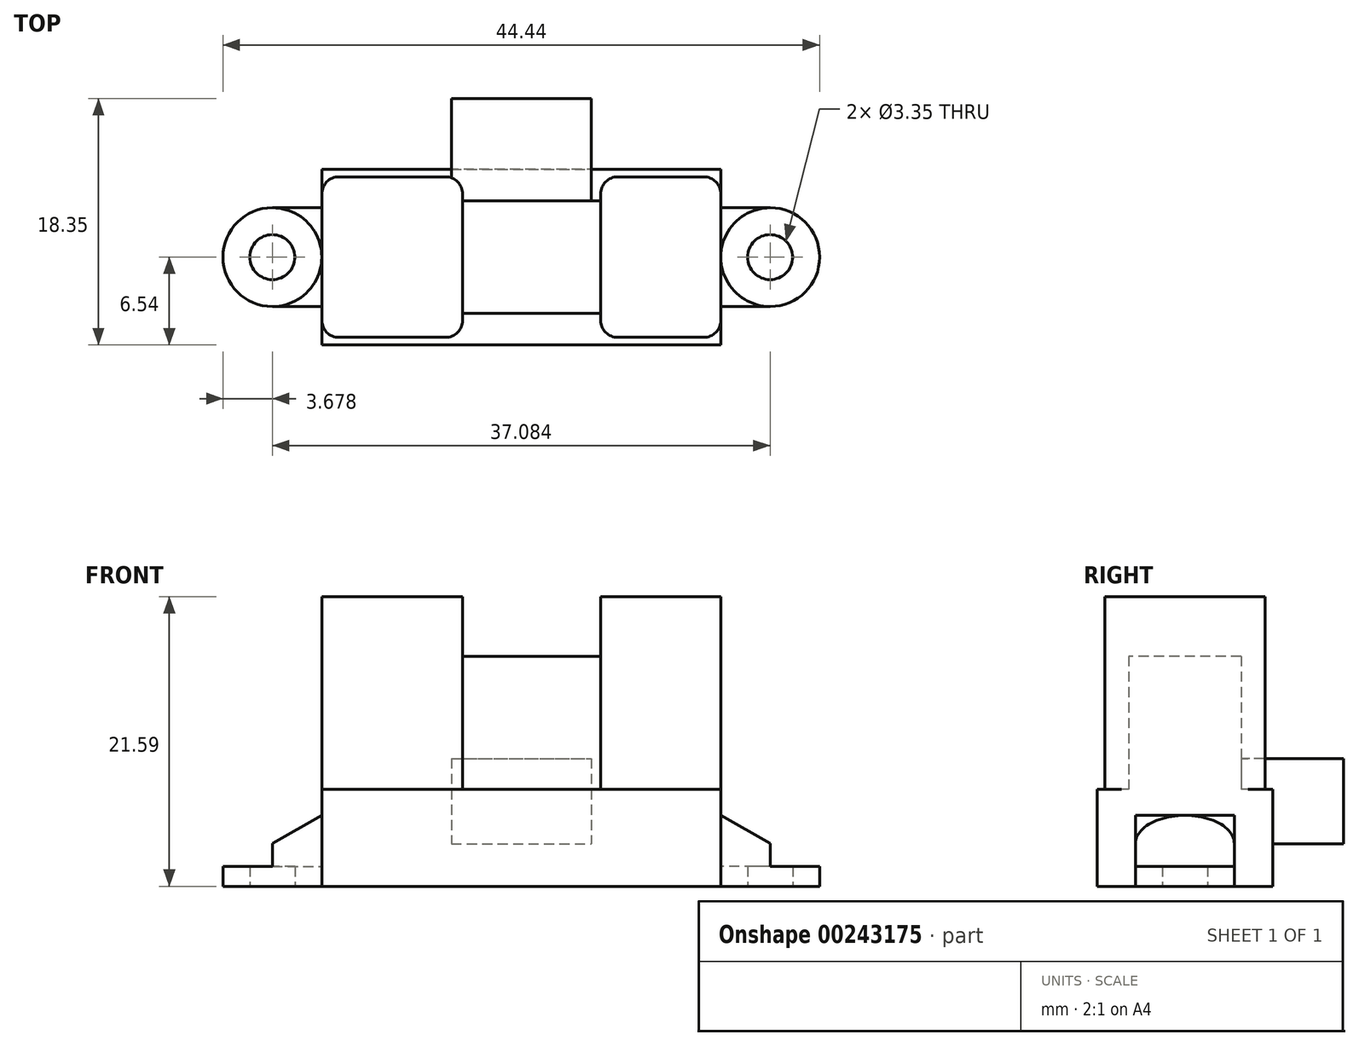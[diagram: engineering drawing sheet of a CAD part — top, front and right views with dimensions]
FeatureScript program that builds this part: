
annotation { "Feature Type Name" : "Feature", "Feature Type Description" : "" }
export const myFeature = defineFeature(function(context is Context, id is Id, definition is map)
    precondition{}
    {
        {
            var Q0;
            Q0=qCreatedBy(makeId("Top.planeOp"),FACE);
            var sketch = newSketch(context, id + "F0", { "sketchPlane" : qUnion([Q0])});
            skLineSegment(sketch, "E0.bottom", {"start": v(14.86, 6.54) * mm, "end": v(-14.86, 6.54) * mm});
            skLineSegment(sketch, "E0.top", {"start": v(14.86, -6.54) * mm, "end": v(-14.86, -6.54) * mm});
            skLineSegment(sketch, "E0.left", {"start": v(14.86, 6.54) * mm, "end": v(14.86, -6.54) * mm});
            skLineSegment(sketch, "E0.right", {"start": v(-14.86, 6.54) * mm, "end": v(-14.86, -6.54) * mm});
            skPoint(sketch, "E0.middle", {"position": v(0, 0) * mm});
            skCircle(sketch, "E1", {"center": v(18.54, 0) * mm, "radius": 3.68 * mm});
            skCircle(sketch, "E2", {"center": v(18.54, 0) * mm, "radius": 1.68 * mm});
            skLineSegment(sketch, "E3", {"start": v(18.54, 3.68) * mm, "end": v(14.86, 3.68) * mm});
            skLineSegment(sketch, "E4", {"start": v(14.86, -3.68) * mm, "end": v(18.54, -3.68) * mm});
            skCircle(sketch, "E5.MirrorC", {"center": v(-18.54, 0) * mm, "radius": 3.68 * mm});
            skLineSegment(sketch, "E6.MirrorCS", {"start": v(-18.54, 3.68) * mm, "end": v(-14.86, 3.68) * mm});
            skCircle(sketch, "E7.MirrorC", {"center": v(-18.54, 0) * mm, "radius": 1.68 * mm});
            skLineSegment(sketch, "E8.MirrorCS", {"start": v(-14.86, -3.68) * mm, "end": v(-18.54, -3.68) * mm});
            skSolve(sketch);
        }
        {
            var Q0;
            Q0=qSketchRegion(id+"F0",true);
            extrude(context, id + "F1", {"entities" : qUnion([Q0]), "depth" : 1.47 * mm});
        }
        {
            var Q0;
            Q0=makeQuery(id+"F1.opExtrude","CAP_FACE",FACE,{"disambiguationData":[OSD([sQuery(id+"F0.wireOp",EDGE,"E0.bottom"),sQuery(id+"F0.wireOp",EDGE,"E0.top"),sQuery(id+"F0.wireOp",EDGE,"E0.left"),sQuery(id+"F0.wireOp",EDGE,"E0.right"),sQuery(id+"F0.wireOp",EDGE,"E1"),sQuery(id+"F0.wireOp",EDGE,"E2"),sQuery(id+"F0.wireOp",EDGE,"E3"),sQuery(id+"F0.wireOp",EDGE,"E4"),sQuery(id+"F0.wireOp",EDGE,"E5.MirrorC"),sQuery(id+"F0.wireOp",EDGE,"E6.MirrorCS"),sQuery(id+"F0.wireOp",EDGE,"E7.MirrorC"),sQuery(id+"F0.wireOp",EDGE,"E8.MirrorCS")])],"isStart":false});
            var sketch = newSketch(context, id + "F2", { "sketchPlane" : qUnion([Q0])});
            skArc(sketch, "E9.0", {"start": v(-18.54, 3.68) * mm, "mid": v(-14.86, 0) * mm, "end": v(-18.54, -3.68) * mm});
            skLineSegment(sketch, "E10.0", {"start": v(-14.86, 3.68) * mm, "end": v(-14.86, -3.68) * mm});
            skArc(sketch, "E11", {"start": v(-18.54, -3.68) * mm, "mid": v(-14.86, 0) * mm, "end": v(-18.54, 3.68) * mm});
            skLineSegment(sketch, "E12.0", {"start": v(-18.54, 3.68) * mm, "end": v(-14.86, 3.68) * mm});
            skLineSegment(sketch, "E13.0", {"start": v(-14.86, -3.68) * mm, "end": v(-18.54, -3.68) * mm});
            skPoint(sketch, "E14.orphan", {"position": v(-14.86, 6.54) * mm});
            skPoint(sketch, "E15.orphan", {"position": v(-14.86, -6.54) * mm});
            skPoint(sketch, "E16.orphan", {"position": v(14.86, -6.54) * mm});
            skPoint(sketch, "E17.orphan", {"position": v(14.86, 6.54) * mm});
            skArc(sketch, "E18.MirrorCS", {"start": v(18.54, -3.68) * mm, "mid": v(14.86, 0) * mm, "end": v(18.54, 3.68) * mm});
            skLineSegment(sketch, "E19.MirrorCS", {"start": v(18.54, 3.68) * mm, "end": v(14.86, 3.68) * mm});
            skLineSegment(sketch, "E20.MirrorCS", {"start": v(14.86, 3.68) * mm, "end": v(14.86, -3.68) * mm});
            skLineSegment(sketch, "E21.MirrorCS", {"start": v(14.86, -3.68) * mm, "end": v(18.54, -3.68) * mm});
            skSolve(sketch);
        }
        {
            var Q0;
            Q0=qSketchRegion(id+"F2",true);
            extrude(context, id + "F3", {"entities" : qUnion([Q0]), "depth" : 3.8 * mm});
        }
        {
            var Q0;
            Q0=makeQuery(id+"F3.opExtrude","SWEPT_FACE",FACE,{"disambiguationData":[OSD([sQuery(id+"F2.wireOp",EDGE,"E13.0")])]});
            var sketch = newSketch(context, id + "F4", { "sketchPlane" : qUnion([Q0])});
            skLineSegment(sketch, "E22", {"start": v(-18.54, 3.2) * mm, "end": v(-18.54, 5.28) * mm});
            skLineSegment(sketch, "E23", {"start": v(-18.54, 3.2) * mm, "end": v(-14.86, 5.28) * mm});
            skLineSegment(sketch, "E24.0", {"start": v(-14.86, 5.28) * mm, "end": v(-18.54, 5.28) * mm});
            skLineSegment(sketch, "E25.MirrorCS", {"start": v(18.54, 3.2) * mm, "end": v(14.86, 5.28) * mm});
            skLineSegment(sketch, "E26.MirrorCS", {"start": v(14.86, 5.28) * mm, "end": v(18.54, 5.28) * mm});
            skLineSegment(sketch, "E27.MirrorCS", {"start": v(18.54, 3.2) * mm, "end": v(18.54, 5.28) * mm});
            skSolve(sketch);
        }
        {
            var Q0;
            Q0=qSketchRegion(id+"F4",true);
            var Q1;
            Q1=makeQuery(id+"F3.opExtrude","SWEPT_FACE",FACE,{"disambiguationData":[OSD([sQuery(id+"F2.wireOp",EDGE,"E12.0")])]});
            extrude(context, id + "F5", {"entities" : qUnion([Q0]), "operationType" : NewBodyOperationType.REMOVE, "endBound" : BoundingType.UP_TO_SURFACE, "oppositeDirection" : true, "endBoundEntityFace" : qUnion([Q1]), "depth" : 25.4 * mm});
        }
        {
            var Q0;
            Q0=qCreatedBy(makeId("Top.planeOp"),FACE);
            var sketch = newSketch(context, id + "F6", { "sketchPlane" : qUnion([Q0])});
            skLineSegment(sketch, "E28.0", {"start": v(14.86, 6.54) * mm, "end": v(-14.86, 6.54) * mm});
            skLineSegment(sketch, "E29.0", {"start": v(-14.86, 6.54) * mm, "end": v(-14.86, 3.68) * mm});
            skLineSegment(sketch, "E30.0", {"start": v(-14.86, 3.68) * mm, "end": v(-14.86, 0) * mm});
            skLineSegment(sketch, "E31.0", {"start": v(-14.86, 0) * mm, "end": v(-14.86, -3.68) * mm});
            skLineSegment(sketch, "E32.0", {"start": v(-14.86, -3.68) * mm, "end": v(-14.86, -6.54) * mm});
            skLineSegment(sketch, "E33.0", {"start": v(14.86, -6.54) * mm, "end": v(-14.86, -6.54) * mm});
            skPoint(sketch, "E34.0", {"position": v(14.86, -5.11) * mm});
            skLineSegment(sketch, "E35.0", {"start": v(14.86, 0) * mm, "end": v(14.86, -3.68) * mm});
            skLineSegment(sketch, "E36.0", {"start": v(14.86, 3.68) * mm, "end": v(14.86, 0) * mm});
            skPoint(sketch, "E37.0", {"position": v(14.86, 5.11) * mm});
            skLineSegment(sketch, "E38.0", {"start": v(14.86, 6.54) * mm, "end": v(14.86, 3.68) * mm});
            skLineSegment(sketch, "E39.0", {"start": v(14.86, -3.68) * mm, "end": v(14.86, -6.54) * mm});
            skSolve(sketch);
        }
        {
            var Q0;
            Q0=qSketchRegion(id+"F6",true);
            extrude(context, id + "F7", {"entities" : qUnion([Q0]), "operationType" : NewBodyOperationType.ADD, "depth" : 7.24 * mm});
        }
        {
            var Q0;
            Q0=makeQuery(id+"F7.opExtrude","CAP_FACE",FACE,{"disambiguationData":[OSD([sQuery(id+"F6.wireOp",EDGE,"E28.0"),sQuery(id+"F6.wireOp",EDGE,"E29.0"),sQuery(id+"F6.wireOp",EDGE,"E30.0"),sQuery(id+"F6.wireOp",EDGE,"E31.0"),sQuery(id+"F6.wireOp",EDGE,"E32.0"),sQuery(id+"F6.wireOp",EDGE,"E33.0"),sQuery(id+"F6.wireOp",EDGE,"E35.0"),sQuery(id+"F6.wireOp",EDGE,"E36.0"),sQuery(id+"F6.wireOp",EDGE,"E38.0"),sQuery(id+"F6.wireOp",EDGE,"E39.0")])],"isStart":false});
            var sketch = newSketch(context, id + "F8", { "sketchPlane" : qUnion([Q0])});
            skLineSegment(sketch, "E40.bottom", {"start": v(-5.64, 5.98) * mm, "end": v(-13.59, 5.98) * mm});
            skLineSegment(sketch, "E40.top", {"start": v(-5.64, -5.98) * mm, "end": v(-13.59, -5.98) * mm});
            skLineSegment(sketch, "E40.left", {"start": v(-4.37, 4.71) * mm, "end": v(-4.37, -4.71) * mm});
            skLineSegment(sketch, "E40.right", {"start": v(-14.86, 4.71) * mm, "end": v(-14.86, -4.71) * mm});
            skPoint(sketch, "E40.middle", {"position": v(-9.61, 0) * mm});
            skPoint(sketch, "E41.visualSharp", {"position": v(-14.86, 5.98) * mm});
            skArc(sketch, "E41.filletArc", {"start": v(-13.59, 5.98) * mm, "mid": v(-14.49, 5.6) * mm, "end": v(-14.86, 4.71) * mm});
            skPoint(sketch, "E42.visualSharp", {"position": v(-4.37, 5.98) * mm});
            skArc(sketch, "E42.filletArc", {"start": v(-4.37, 4.71) * mm, "mid": v(-4.74, 5.6) * mm, "end": v(-5.64, 5.98) * mm});
            skPoint(sketch, "E43.visualSharp", {"position": v(-4.37, -5.98) * mm});
            skArc(sketch, "E43.filletArc", {"start": v(-5.64, -5.98) * mm, "mid": v(-4.74, -5.6) * mm, "end": v(-4.37, -4.71) * mm});
            skPoint(sketch, "E44.visualSharp", {"position": v(-14.86, -5.98) * mm});
            skArc(sketch, "E44.filletArc", {"start": v(-14.86, -4.71) * mm, "mid": v(-14.49, -5.6) * mm, "end": v(-13.59, -5.98) * mm});
            skLineSegment(sketch, "E45.bottom", {"start": v(13.59, 5.98) * mm, "end": v(7.19, 5.98) * mm});
            skLineSegment(sketch, "E45.top", {"start": v(13.59, -5.98) * mm, "end": v(7.19, -5.98) * mm});
            skLineSegment(sketch, "E45.left", {"start": v(14.86, 4.71) * mm, "end": v(14.86, -4.71) * mm});
            skLineSegment(sketch, "E45.right", {"start": v(5.92, 4.71) * mm, "end": v(5.92, -4.71) * mm});
            skPoint(sketch, "E45.middle", {"position": v(10.39, 0) * mm});
            skPoint(sketch, "E46.visualSharp", {"position": v(5.92, 5.98) * mm});
            skArc(sketch, "E46.filletArc", {"start": v(7.19, 5.98) * mm, "mid": v(6.3, 5.6) * mm, "end": v(5.92, 4.71) * mm});
            skPoint(sketch, "E47.visualSharp", {"position": v(14.86, 5.98) * mm});
            skArc(sketch, "E47.filletArc", {"start": v(14.86, 4.71) * mm, "mid": v(14.49, 5.6) * mm, "end": v(13.59, 5.98) * mm});
            skPoint(sketch, "E48.visualSharp", {"position": v(14.86, -5.98) * mm});
            skArc(sketch, "E48.filletArc", {"start": v(13.59, -5.98) * mm, "mid": v(14.49, -5.6) * mm, "end": v(14.86, -4.71) * mm});
            skPoint(sketch, "E49.visualSharp", {"position": v(5.92, -5.98) * mm});
            skArc(sketch, "E49.filletArc", {"start": v(5.92, -4.71) * mm, "mid": v(6.3, -5.6) * mm, "end": v(7.19, -5.98) * mm});
            skSolve(sketch);
        }
        {
            var Q0;
            Q0=qSketchRegion(id+"F8",true);
            extrude(context, id + "F9", {"entities" : qUnion([Q0]), "operationType" : NewBodyOperationType.ADD, "depth" : 14.35 * mm});
        }
        {
            var Q0;
            Q0=makeQuery(id+"F7.opExtrude","CAP_FACE",FACE,{"disambiguationData":[OSD([sQuery(id+"F6.wireOp",EDGE,"E28.0"),sQuery(id+"F6.wireOp",EDGE,"E29.0"),sQuery(id+"F6.wireOp",EDGE,"E30.0"),sQuery(id+"F6.wireOp",EDGE,"E31.0"),sQuery(id+"F6.wireOp",EDGE,"E32.0"),sQuery(id+"F6.wireOp",EDGE,"E33.0"),sQuery(id+"F6.wireOp",EDGE,"E35.0"),sQuery(id+"F6.wireOp",EDGE,"E36.0"),sQuery(id+"F6.wireOp",EDGE,"E38.0"),sQuery(id+"F6.wireOp",EDGE,"E39.0")])],"isStart":false});
            var sketch = newSketch(context, id + "F10", { "sketchPlane" : qUnion([Q0])});
            skLineSegment(sketch, "E50.bottom", {"start": v(5.92, 4.2) * mm, "end": v(-4.37, 4.2) * mm});
            skLineSegment(sketch, "E50.top", {"start": v(5.92, -4.2) * mm, "end": v(-4.37, -4.2) * mm});
            skLineSegment(sketch, "E50.left", {"start": v(5.92, 4.2) * mm, "end": v(5.92, -4.2) * mm});
            skLineSegment(sketch, "E50.right", {"start": v(-4.37, 4.2) * mm, "end": v(-4.37, -4.2) * mm});
            skPoint(sketch, "E50.middle", {"position": v(0.77, 0) * mm});
            skSolve(sketch);
        }
        {
            var Q0;
            Q0=qSketchRegion(id+"F10",true);
            extrude(context, id + "F11", {"entities" : qUnion([Q0]), "operationType" : NewBodyOperationType.ADD, "depth" : 9.9 * mm});
        }
        {
            var Q0;
            Q0=makeQuery(id+"F11.opExtrude","SWEPT_FACE",FACE,{"disambiguationData":[OSD([sQuery(id+"F10.wireOp",EDGE,"E50.bottom")])]});
            var sketch = newSketch(context, id + "F12", { "sketchPlane" : qUnion([Q0])});
            skLineSegment(sketch, "E51.bottom", {"start": v(5.2, 9.53) * mm, "end": v(-5.2, 9.53) * mm});
            skLineSegment(sketch, "E51.top", {"start": v(5.2, 3.18) * mm, "end": v(-5.2, 3.18) * mm});
            skLineSegment(sketch, "E51.left", {"start": v(5.2, 9.53) * mm, "end": v(5.2, 3.18) * mm});
            skLineSegment(sketch, "E51.right", {"start": v(-5.2, 9.53) * mm, "end": v(-5.2, 3.18) * mm});
            skPoint(sketch, "E51.middle", {"position": v(0, 6.35) * mm});
            skSolve(sketch);
        }
        {
            var Q0;
            Q0=qSketchRegion(id+"F12",true);
            extrude(context, id + "F13", {"entities" : qUnion([Q0]), "operationType" : NewBodyOperationType.ADD, "depth" : 7.62 * mm});
        }
    });
